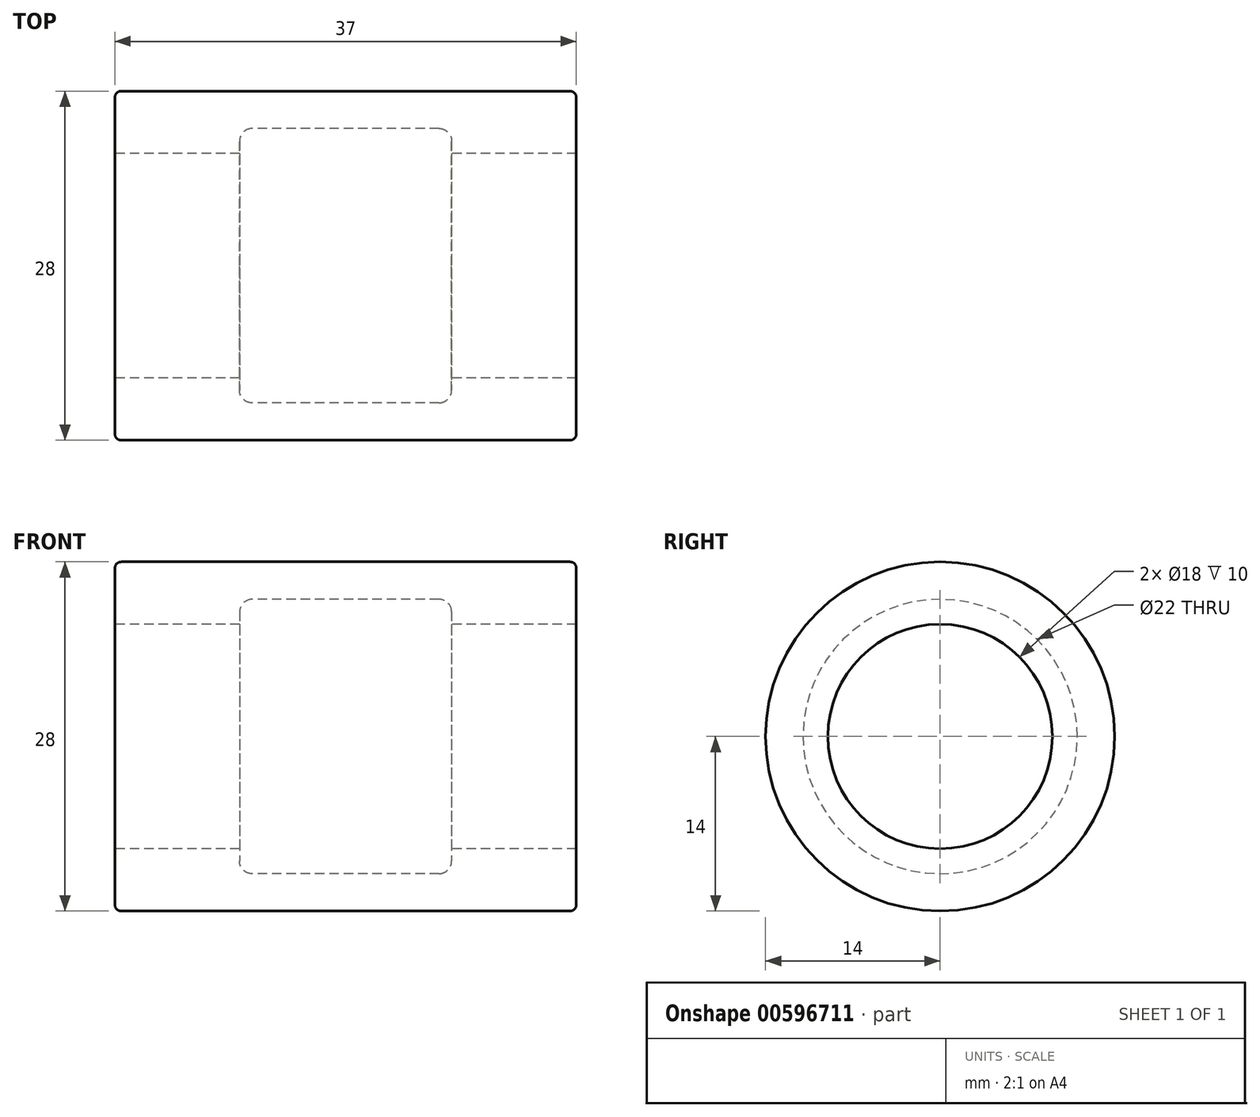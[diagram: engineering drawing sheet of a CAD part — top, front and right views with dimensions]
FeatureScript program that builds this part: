
annotation { "Feature Type Name" : "Feature", "Feature Type Description" : "" }
export const myFeature = defineFeature(function(context is Context, id is Id, definition is map)
    precondition{}
    {
        {
            var Q0;
            Q0=qCreatedBy(makeId("Front.planeOp"),FACE);
            var sketch = newSketch(context, id + "F0", { "sketchPlane" : qUnion([Q0])});
            skLineSegment(sketch, "E0", {"start": v(-2.15, 0) * mm, "end": v(1.9, 0) * mm, "construction": true});
            skLineSegment(sketch, "E1", {"start": v(-2.66, 14) * mm, "end": v(34.34, 14) * mm});
            skLineSegment(sketch, "E2", {"start": v(-2.66, 14) * mm, "end": v(-2.66, 9) * mm});
            skLineSegment(sketch, "E3", {"start": v(-2.66, 9) * mm, "end": v(7.34, 9) * mm});
            skLineSegment(sketch, "E4", {"start": v(7.34, 9) * mm, "end": v(7.34, 10) * mm});
            skLineSegment(sketch, "E5", {"start": v(8.34, 11) * mm, "end": v(23.34, 11) * mm});
            skLineSegment(sketch, "E6", {"start": v(24.34, 10) * mm, "end": v(24.34, 9) * mm});
            skLineSegment(sketch, "E7", {"start": v(24.34, 9) * mm, "end": v(34.34, 9) * mm});
            skLineSegment(sketch, "E8", {"start": v(34.34, 9) * mm, "end": v(34.34, 14) * mm});
            skPoint(sketch, "E9.visualSharp", {"position": v(7.34, 11) * mm});
            skArc(sketch, "E9.filletArc", {"start": v(8.34, 11) * mm, "mid": v(7.63, 10.7) * mm, "end": v(7.34, 10) * mm});
            skPoint(sketch, "E10.visualSharp", {"position": v(24.34, 11) * mm});
            skArc(sketch, "E10.filletArc", {"start": v(24.34, 10) * mm, "mid": v(24.05, 10.7) * mm, "end": v(23.34, 11) * mm});
            skSolve(sketch);
        }
        {
            var Q0;
            Q0=makeQuery(id+"F0.imprint","IMPRINT",FACE,{"disambiguationData":[TD([[makeQuery(id+"F0.imprint","IMPRINT",EDGE,{"derivedFrom":sQuery(id+"F0.wireOp",EDGE,"E1")}),-1.0]])]});
            var Q1;
            Q1=sQuery(id+"F0.wireOp",EDGE,"E0");
            revolve(context, id + "F1", {"entities" : qUnion([Q0]), "axis" : qUnion([Q1]), "revolveType" : RevolveType.FULL});
        }
        {
            var Q0;
            Q0=makeQuery(id+"F1.opRevolve","SWEPT_EDGE",EDGE,{"disambiguationData":[OSD([sQuery(id+"F0.wireOp",EDGE,"E1"),sQuery(id+"F0.wireOp",EDGE,"E2")])]});
            var Q1;
            Q1=makeQuery(id+"F1.opRevolve","SWEPT_EDGE",EDGE,{"disambiguationData":[OSD([sQuery(id+"F0.wireOp",EDGE,"E1"),sQuery(id+"F0.wireOp",EDGE,"E8")])]});
            fillet(context, id + "F2", {"entities" : qUnion([Q0, Q1]), "radius" : 0.5 * mm, "tangentPropagation" : true, "allowEdgeOverflow" : false});
        }
    });
